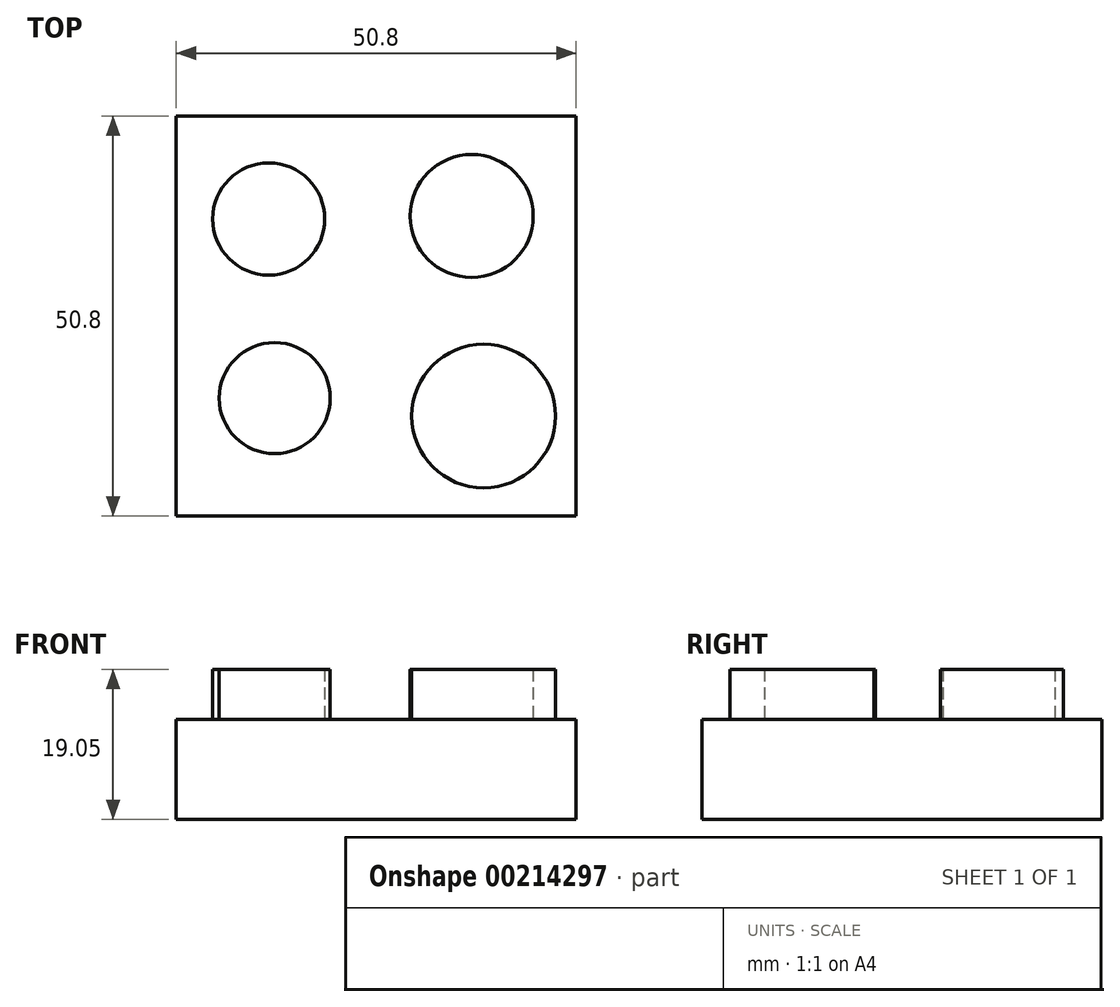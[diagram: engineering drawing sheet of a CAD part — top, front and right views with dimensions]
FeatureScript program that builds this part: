
annotation { "Feature Type Name" : "Feature", "Feature Type Description" : "" }
export const myFeature = defineFeature(function(context is Context, id is Id, definition is map)
    precondition{}
    {
        {
            var Q0;
            Q0=qCreatedBy(makeId("Top.planeOp"),FACE);
            var sketch = newSketch(context, id + "F0", { "sketchPlane" : qUnion([Q0])});
            skLineSegment(sketch, "E0.bottom", {"start": v(-25.4, 25.4) * mm, "end": v(25.4, 25.4) * mm});
            skLineSegment(sketch, "E0.top", {"start": v(-25.4, -25.4) * mm, "end": v(25.4, -25.4) * mm});
            skLineSegment(sketch, "E0.left", {"start": v(-25.4, 25.4) * mm, "end": v(-25.4, -25.4) * mm});
            skLineSegment(sketch, "E0.right", {"start": v(25.4, 25.4) * mm, "end": v(25.4, -25.4) * mm});
            skPoint(sketch, "E0.middle", {"position": v(0, 0) * mm});
            skSolve(sketch);
        }
        {
            var Q0;
            Q0=makeQuery(id+"F0.imprint","IMPRINT",FACE,{"disambiguationData":[TD([[makeQuery(id+"F0.imprint","IMPRINT",EDGE,{"derivedFrom":sQuery(id+"F0.wireOp",EDGE,"E0.bottom")}),-1.0]])]});
            extrude(context, id + "F1", {"entities" : qUnion([Q0]), "depth" : 12.7 * mm});
        }
        {
            var Q0;
            Q0=makeQuery(id+"F1.opExtrude","CAP_FACE",FACE,{"disambiguationData":[OSD([sQuery(id+"F0.wireOp",EDGE,"E0.bottom"),sQuery(id+"F0.wireOp",EDGE,"E0.top"),sQuery(id+"F0.wireOp",EDGE,"E0.left"),sQuery(id+"F0.wireOp",EDGE,"E0.right")])],"isStart":false});
            var sketch = newSketch(context, id + "F2", { "sketchPlane" : qUnion([Q0])});
            skCircle(sketch, "E1", {"center": v(-13.65, 12.32) * mm, "radius": 7.12 * mm});
            skCircle(sketch, "E2", {"center": v(12.13, 12.7) * mm, "radius": 7.82 * mm});
            skCircle(sketch, "E3", {"center": v(-12.9, -10.43) * mm, "radius": 7.05 * mm});
            skCircle(sketch, "E4", {"center": v(13.65, -12.7) * mm, "radius": 9.13 * mm});
            skSolve(sketch);
        }
        {
            var Q0;
            Q0=makeQuery(id+"F2.imprint","IMPRINT",FACE,{"disambiguationData":[TD([[makeQuery(id+"F2.imprint","IMPRINT",EDGE,{"derivedFrom":sQuery(id+"F2.wireOp",EDGE,"E1")}),1.0]])]});
            extrude(context, id + "F3", {"entities" : qUnion([Q0]), "operationType" : NewBodyOperationType.ADD, "depth" : 6.35 * mm});
        }
        {
            var Q0;
            Q0=makeQuery(id+"F2.imprint","IMPRINT",FACE,{"disambiguationData":[TD([[makeQuery(id+"F2.imprint","IMPRINT",EDGE,{"derivedFrom":sQuery(id+"F2.wireOp",EDGE,"E2")}),1.0]])]});
            extrude(context, id + "F4", {"entities" : qUnion([Q0]), "operationType" : NewBodyOperationType.ADD, "depth" : 6.35 * mm});
        }
        {
            var Q0;
            Q0=makeQuery(id+"F2.imprint","IMPRINT",FACE,{"disambiguationData":[TD([[makeQuery(id+"F2.imprint","IMPRINT",EDGE,{"derivedFrom":sQuery(id+"F2.wireOp",EDGE,"E3")}),1.0]])]});
            extrude(context, id + "F5", {"entities" : qUnion([Q0]), "operationType" : NewBodyOperationType.ADD, "depth" : 6.35 * mm});
        }
        {
            var Q0;
            Q0=makeQuery(id+"F2.imprint","IMPRINT",FACE,{"disambiguationData":[TD([[makeQuery(id+"F2.imprint","IMPRINT",EDGE,{"derivedFrom":sQuery(id+"F2.wireOp",EDGE,"E4")}),1.0]])]});
            extrude(context, id + "F6", {"entities" : qUnion([Q0]), "operationType" : NewBodyOperationType.ADD, "depth" : 6.35 * mm});
        }
    });
